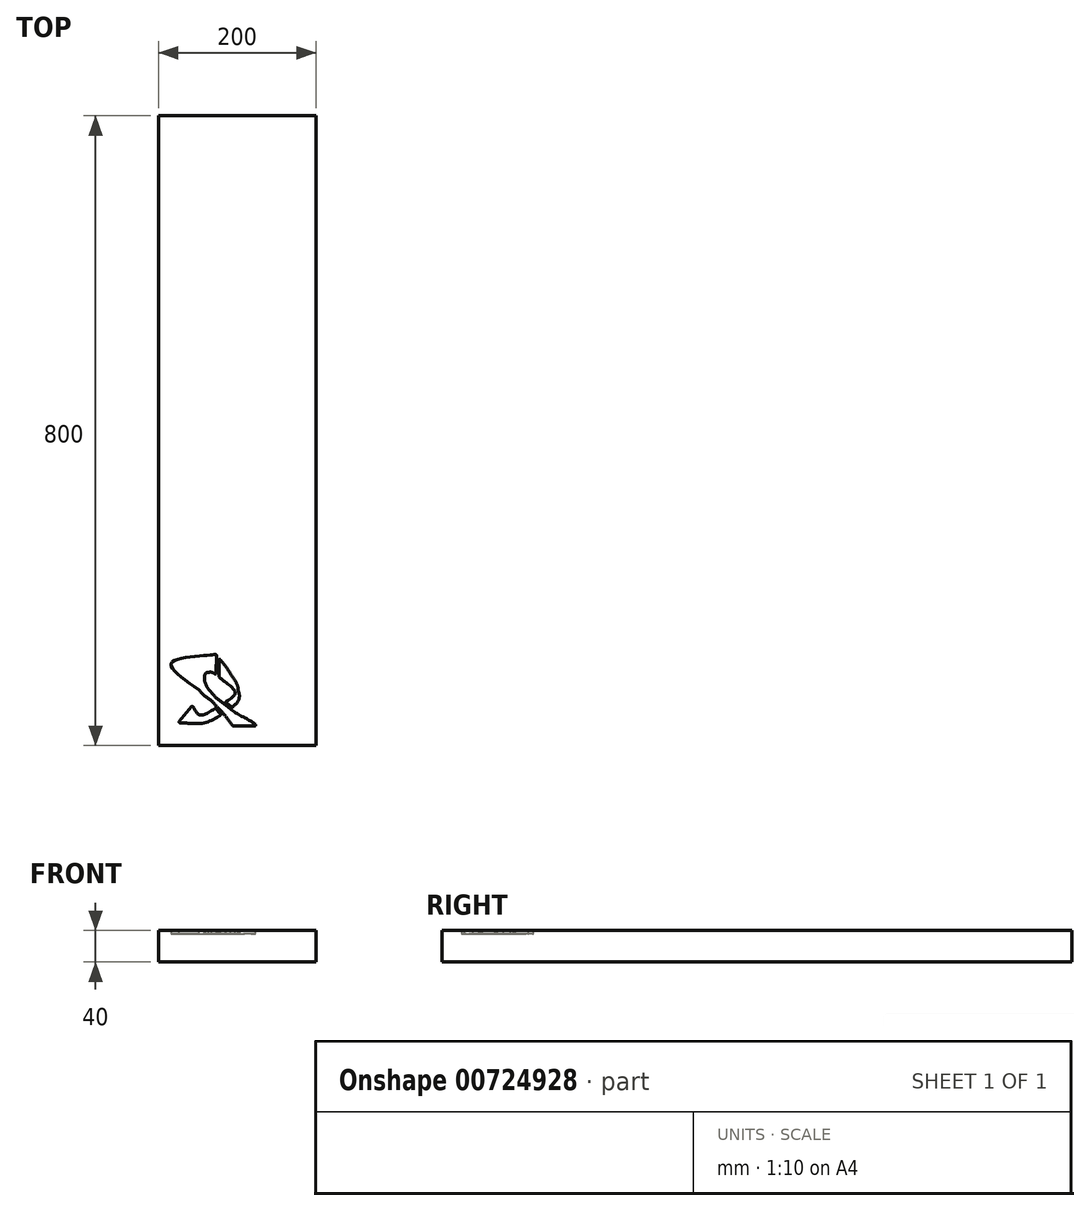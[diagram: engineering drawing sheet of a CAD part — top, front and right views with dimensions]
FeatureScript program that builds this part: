
annotation { "Feature Type Name" : "Feature", "Feature Type Description" : "" }
export const myFeature = defineFeature(function(context is Context, id is Id, definition is map)
    precondition{}
    {
        {
            var Q0;
            Q0=qCreatedBy(makeId("Top.planeOp"),FACE);
            var sketch = newSketch(context, id + "F0", { "sketchPlane" : qUnion([Q0])});
            skLineSegment(sketch, "E0.bottom", {"start": v(0, 0) * mm, "end": v(200, 0) * mm});
            skLineSegment(sketch, "E0.top", {"start": v(0, 800) * mm, "end": v(200, 800) * mm});
            skLineSegment(sketch, "E0.left", {"start": v(0, 0) * mm, "end": v(0, 800) * mm});
            skLineSegment(sketch, "E0.right", {"start": v(200, 0) * mm, "end": v(200, 800) * mm});
            skSolve(sketch);
        }
        {
            var Q0;
            Q0=makeQuery(id+"F0.imprint","IMPRINT",FACE,{"disambiguationData":[TD([[makeQuery(id+"F0.imprint","IMPRINT",EDGE,{"derivedFrom":sQuery(id+"F0.wireOp",EDGE,"E0.bottom")}),1.0]])]});
            extrude(context, id + "F1", {"entities" : qUnion([Q0]), "oppositeDirection" : true, "depth" : 40 * mm, "offsetDistance" : 25 * mm});
        }
        {
            var Q0;
            Q0=makeQuery(id+"F1.opExtrude","CAP_FACE",FACE,{"disambiguationData":[OSD([sQuery(id+"F0.wireOp",EDGE,"E0.bottom"),sQuery(id+"F0.wireOp",EDGE,"E0.top"),sQuery(id+"F0.wireOp",EDGE,"E0.left"),sQuery(id+"F0.wireOp",EDGE,"E0.right")])],"isStart":true});
            var sketch = newSketch(context, id + "F2", { "sketchPlane" : qUnion([Q0])});
            skLineSegment(sketch, "E1", {"start": v(93.99, 24.95) * mm, "end": v(124.87, 24.95) * mm});
            skLineSegment(sketch, "E2", {"start": v(73.32, 89.57) * mm, "end": v(73.39, 116.14) * mm});
            skLineSegment(sketch, "E3", {"start": v(76.6, 111.65) * mm, "end": v(76.7, 87.26) * mm});
            skLineSegment(sketch, "E4", {"start": v(42.57, 50.36) * mm, "end": v(24.87, 28.96) * mm});
            skFitSpline(sketch, "E5", {"points": [v(73.39, 116.14) * mm, v(61.26, 114.57) * mm, v(16.6, 105.32) * mm, v(51.41, 70.54) * mm]});
            skFitSpline(sketch, "E6", {"points": [v(51.41, 70.54) * mm, v(59.7, 62.05) * mm, v(65.6, 58.22) * mm, v(74.01, 49.46) * mm]});
            skFitSpline(sketch, "E7", {"points": [v(74.01, 49.46) * mm, v(79.28, 44) * mm, v(85.53, 36.6) * mm, v(93.99, 24.95) * mm]});
            skFitSpline(sketch, "E8", {"points": [v(124.87, 24.95) * mm, v(117.37, 30.86) * mm, v(100.1, 40.5) * mm, v(85.05, 51.62) * mm]});
            skFitSpline(sketch, "E9", {"points": [v(85.05, 51.62) * mm, v(78.32, 56.58) * mm, v(72.04, 61.84) * mm, v(67.26, 67.19) * mm]});
            skFitSpline(sketch, "E10", {"points": [v(67.26, 67.19) * mm, v(64.01, 70.83) * mm, v(61.46, 74.5) * mm, v(59.94, 78.16) * mm]});
            skFitSpline(sketch, "E11", {"points": [v(59.94, 78.16) * mm, v(58.68, 81.18) * mm, v(58.13, 84.18) * mm, v(58.47, 87.13) * mm]});
            skFitSpline(sketch, "E12", {"points": [v(58.47, 87.13) * mm, v(58.85, 90.28) * mm, v(60.7, 92.48) * mm, v(63.6, 92.94) * mm]});
            skFitSpline(sketch, "E13", {"points": [v(63.6, 92.94) * mm, v(66.15, 93.34) * mm, v(69.49, 92.4) * mm, v(73.32, 89.57) * mm]});
            skFitSpline(sketch, "E14", {"points": [v(76.7, 87.26) * mm, v(83.87, 81.35) * mm, v(97.25, 67.4) * mm, v(84.63, 55.42) * mm]});
            skFitSpline(sketch, "E15", {"points": [v(84.63, 55.42) * mm, v(87.75, 52.95) * mm, v(90.15, 51.2) * mm, v(93.67, 48.84) * mm]});
            skFitSpline(sketch, "E16", {"points": [v(93.67, 48.84) * mm, v(99.72, 54.77) * mm, v(102.64, 62.43) * mm, v(101.2, 70.09) * mm]});
            skFitSpline(sketch, "E17", {"points": [v(101.2, 70.09) * mm, v(100.34, 76.03) * mm, v(96.49, 83.38) * mm, v(91.66, 90.82) * mm]});
            skFitSpline(sketch, "E18", {"points": [v(91.66, 90.82) * mm, v(86.95, 98.09) * mm, v(81.3, 105.44) * mm, v(76.6, 111.65) * mm]});
            skFitSpline(sketch, "E19", {"points": [v(24.87, 28.96) * mm, v(35.18, 28.6) * mm, v(57.7, 28.8) * mm, v(79.23, 38.83) * mm]});
            skFitSpline(sketch, "E20", {"points": [v(79.23, 38.83) * mm, v(77.16, 41.68) * mm, v(74.34, 44.8) * mm, v(72, 47.26) * mm]});
            skFitSpline(sketch, "E21", {"points": [v(72, 47.26) * mm, v(51.47, 39.23) * mm, v(44.75, 48.17) * mm, v(42.57, 50.36) * mm]});
            skSolve(sketch);
        }
        {
            var Q0;
            Q0 = qSketchRegion(id + "F2", true);
            extrude(context, id + "F3", {"entities" : qUnion([Q0]), "operationType" : NewBodyOperationType.REMOVE, "oppositeDirection" : true, "depth" : 4 * mm, "offsetDistance" : 25 * mm});
        }
        {
            var Q0;
            Q0=makeQuery(id+"F3.boolean.opBoolean","COPY",EDGE,{"derivedFrom":makeQuery(id+"F3.opExtrude","SWEPT_EDGE",EDGE,{"disambiguationData":[OSD([sQuery(id+"F2.wireOp",EDGE,"E2"),sQuery(id+"F2.wireOp",EDGE,"E5")])]})});
            var Q1;
            Q1=makeQuery(id+"F3.boolean.opBoolean","COPY",EDGE,{"derivedFrom":makeQuery(id+"F3.opExtrude","SWEPT_EDGE",EDGE,{"disambiguationData":[OSD([sQuery(id+"F2.wireOp",EDGE,"E2"),sQuery(id+"F2.wireOp",EDGE,"E13")])]})});
            var Q2;
            Q2=makeQuery(id+"F3.boolean.opBoolean","COPY",EDGE,{"derivedFrom":makeQuery(id+"F3.opExtrude","SWEPT_EDGE",EDGE,{"disambiguationData":[OSD([sQuery(id+"F2.wireOp",EDGE,"E3"),sQuery(id+"F2.wireOp",EDGE,"E14")])]})});
            var Q3;
            Q3=makeQuery(id+"F3.boolean.opBoolean","COPY",EDGE,{"derivedFrom":makeQuery(id+"F3.opExtrude","SWEPT_EDGE",EDGE,{"disambiguationData":[OSD([sQuery(id+"F2.wireOp",EDGE,"E3"),sQuery(id+"F2.wireOp",EDGE,"E18")])]})});
            var Q4;
            Q4=makeQuery(id+"F3.boolean.opBoolean","COPY",EDGE,{"derivedFrom":makeQuery(id+"F3.opExtrude","SWEPT_EDGE",EDGE,{"disambiguationData":[OSD([sQuery(id+"F2.wireOp",EDGE,"E15"),sQuery(id+"F2.wireOp",EDGE,"E16")])]})});
            var Q5;
            Q5=makeQuery(id+"F3.boolean.opBoolean","COPY",EDGE,{"derivedFrom":makeQuery(id+"F3.opExtrude","SWEPT_EDGE",EDGE,{"disambiguationData":[OSD([sQuery(id+"F2.wireOp",EDGE,"E14"),sQuery(id+"F2.wireOp",EDGE,"E15")])]})});
            var Q6;
            Q6=makeQuery(id+"F3.boolean.opBoolean","COPY",EDGE,{"derivedFrom":makeQuery(id+"F3.opExtrude","SWEPT_EDGE",EDGE,{"disambiguationData":[OSD([sQuery(id+"F2.wireOp",EDGE,"E1"),sQuery(id+"F2.wireOp",EDGE,"E8")])]})});
            var Q7;
            Q7=makeQuery(id+"F3.boolean.opBoolean","COPY",EDGE,{"derivedFrom":makeQuery(id+"F3.opExtrude","SWEPT_EDGE",EDGE,{"disambiguationData":[OSD([sQuery(id+"F2.wireOp",EDGE,"E1"),sQuery(id+"F2.wireOp",EDGE,"E7")])]})});
            var Q8;
            Q8=makeQuery(id+"F3.boolean.opBoolean","COPY",EDGE,{"derivedFrom":makeQuery(id+"F3.opExtrude","SWEPT_EDGE",EDGE,{"disambiguationData":[OSD([sQuery(id+"F2.wireOp",EDGE,"E4"),sQuery(id+"F2.wireOp",EDGE,"E21")])]})});
            var Q9;
            Q9=makeQuery(id+"F3.boolean.opBoolean","COPY",EDGE,{"derivedFrom":makeQuery(id+"F3.opExtrude","SWEPT_EDGE",EDGE,{"disambiguationData":[OSD([sQuery(id+"F2.wireOp",EDGE,"E20"),sQuery(id+"F2.wireOp",EDGE,"E21")])]})});
            var Q10;
            Q10=makeQuery(id+"F3.boolean.opBoolean","COPY",EDGE,{"derivedFrom":makeQuery(id+"F3.opExtrude","SWEPT_EDGE",EDGE,{"disambiguationData":[OSD([sQuery(id+"F2.wireOp",EDGE,"E19"),sQuery(id+"F2.wireOp",EDGE,"E20")])]})});
            var Q11;
            Q11=makeQuery(id+"F3.boolean.opBoolean","COPY",EDGE,{"derivedFrom":makeQuery(id+"F3.opExtrude","SWEPT_EDGE",EDGE,{"disambiguationData":[OSD([sQuery(id+"F2.wireOp",EDGE,"E4"),sQuery(id+"F2.wireOp",EDGE,"E19")])]})});
            fillet(context, id + "F4", {"entities" : qUnion([Q0, Q1, Q2, Q3, Q4, Q5, Q6, Q7, Q8, Q9, Q10, Q11]), "tangentPropagation" : true, "radius" : 1 * mm, "defaultsChanged" : false, "vertexSettings" : [], "allowEdgeOverflow" : false});
        }
    });
